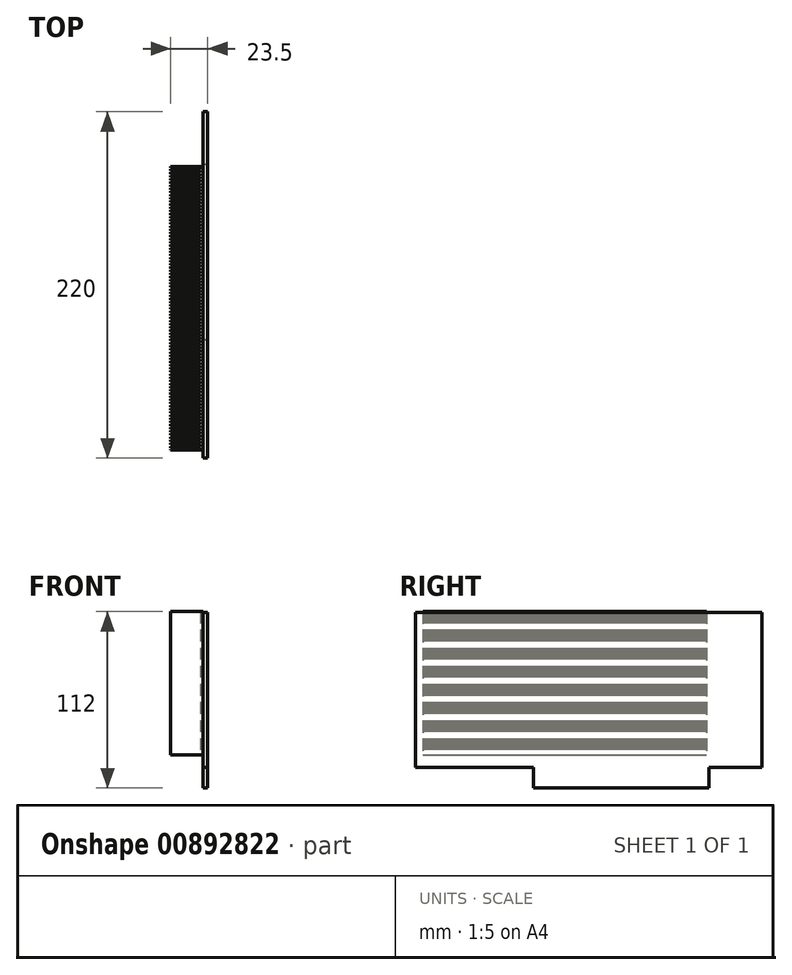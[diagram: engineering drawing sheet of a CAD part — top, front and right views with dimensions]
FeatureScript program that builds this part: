
annotation { "Feature Type Name" : "Feature", "Feature Type Description" : "" }
export const myFeature = defineFeature(function(context is Context, id is Id, definition is map)
    precondition{}
    {
        {
            var Q0;
            Q0=qCreatedBy(makeId("Right.planeOp"),FACE);
            var sketch = newSketch(context, id + "F0", { "sketchPlane" : qUnion([Q0])});
            skLineSegment(sketch, "E0.bottom", {"start": v(-110, 55.75) * mm, "end": v(110, 55.75) * mm});
            skLineSegment(sketch, "E0.top", {"start": v(-35, -55.75) * mm, "end": v(76.5, -55.75) * mm});
            skLineSegment(sketch, "E0.left", {"start": v(-110, 55.75) * mm, "end": v(-110, -42.75) * mm});
            skLineSegment(sketch, "E0.right", {"start": v(110, 55.75) * mm, "end": v(110, -42.75) * mm});
            skPoint(sketch, "E0.middle", {"position": v(0, 0) * mm});
            skLineSegment(sketch, "E1", {"start": v(-110, -42.75) * mm, "end": v(-35, -42.75) * mm});
            skLineSegment(sketch, "E2", {"start": v(-35, -42.75) * mm, "end": v(-35, -55.75) * mm});
            skLineSegment(sketch, "E3", {"start": v(76.5, -55.75) * mm, "end": v(76.5, -42.75) * mm});
            skLineSegment(sketch, "E4", {"start": v(76.5, -42.75) * mm, "end": v(110, -42.75) * mm});
            skLineSegment(sketch, "E5.bottom", {"start": v(-105, 56.25) * mm, "end": v(75, 56.25) * mm});
            skLineSegment(sketch, "E5.top", {"start": v(-105, -34.75) * mm, "end": v(75, -34.75) * mm});
            skLineSegment(sketch, "E5.left", {"start": v(-105, 56.25) * mm, "end": v(-105, -34.75) * mm});
            skLineSegment(sketch, "E5.right", {"start": v(75, 56.25) * mm, "end": v(75, -34.75) * mm});
            skSolve(sketch);
        }
        {
            var Q0;
            Q0=makeQuery(id+"F0.imprint","IMPRINT",FACE,{"disambiguationData":[TD([[makeQuery(id+"F0.imprint","IMPRINT",EDGE,{"derivedFrom":sQuery(id+"F0.wireOp",EDGE,"E0.top")}),1.0]])]});
            extrude(context, id + "F1", {"entities" : qUnion([Q0]), "depth" : 3 * mm, "offsetDistance" : 25 * mm});
        }
        {
            var Q0;
            {var subQ5=sQuery(id+"F0.wireOp",EDGE,"E5.top");Q0=makeQuery(id+"F0.imprint","IMPRINT",FACE,{"disambiguationData":[TD([[makeQuery(id+"F0.imprint","IMPRINT",EDGE,{"derivedFrom":subQ5}),1.0]])]});}
            extrude(context, id + "F2", {"entities" : qUnion([Q0]), "operationType" : NewBodyOperationType.ADD, "depth" : 3 * mm, "offsetDistance" : 25 * mm});
        }
        {
            var Q0;
            {var subQ5=sQuery(id+"F0.wireOp",EDGE,"E5.bottom");Q0=makeQuery(id+"F0.imprint","IMPRINT",FACE,{"disambiguationData":[TD([[makeQuery(id+"F0.imprint","IMPRINT",EDGE,{"derivedFrom":subQ5}),-1.0]])]});}
            var Q1;
            {var subQ5=sQuery(id+"F0.wireOp",EDGE,"E5.top");Q1=makeQuery(id+"F0.imprint","IMPRINT",FACE,{"disambiguationData":[TD([[makeQuery(id+"F0.imprint","IMPRINT",EDGE,{"derivedFrom":subQ5}),1.0]])]});}
            extrude(context, id + "F3", {"entities" : qUnion([Q0, Q1]), "operationType" : NewBodyOperationType.ADD, "depth" : -20.5 * mm, "offsetDistance" : 25 * mm});
        }
        {
            var Q0;
            Q0=makeQuery(id+"F3.opExtrude","CAP_FACE",FACE,{"disambiguationData":[OSD([sQuery(id+"F0.wireOp",EDGE,"E5.bottom"),sQuery(id+"F0.wireOp",EDGE,"E5.top"),sQuery(id+"F0.wireOp",EDGE,"E5.left"),sQuery(id+"F0.wireOp",EDGE,"E5.right")])],"isStart":false});
            var sketch = newSketch(context, id + "F4", { "sketchPlane" : qUnion([Q0])});
            skLineSegment(sketch, "E6.bottom", {"start": v(-74.5, 56.25) * mm, "end": v(-73.5, 56.25) * mm});
            skLineSegment(sketch, "E6.top", {"start": v(-74.5, -34.75) * mm, "end": v(-73.5, -34.75) * mm});
            skLineSegment(sketch, "E6.left", {"start": v(-74.5, 56.25) * mm, "end": v(-74.5, -34.75) * mm});
            skLineSegment(sketch, "E6.right", {"start": v(-73.5, 56.25) * mm, "end": v(-73.5, -34.75) * mm});
            skLineSegment(sketch, "E7.1.0.0", {"start": v(-72.5, 56.25) * mm, "end": v(-71.5, 56.25) * mm});
            skLineSegment(sketch, "E7.1.0.1", {"start": v(-72.5, -34.75) * mm, "end": v(-71.5, -34.75) * mm});
            skLineSegment(sketch, "E7.1.0.2", {"start": v(-72.5, 56.25) * mm, "end": v(-72.5, -34.75) * mm});
            skLineSegment(sketch, "E7.1.0.3", {"start": v(-71.5, 56.25) * mm, "end": v(-71.5, -34.75) * mm});
            skLineSegment(sketch, "E7.2.0.0", {"start": v(-70.5, 56.25) * mm, "end": v(-69.5, 56.25) * mm});
            skLineSegment(sketch, "E7.2.0.1", {"start": v(-70.5, -34.75) * mm, "end": v(-69.5, -34.75) * mm});
            skLineSegment(sketch, "E7.2.0.2", {"start": v(-70.5, 56.25) * mm, "end": v(-70.5, -34.75) * mm});
            skLineSegment(sketch, "E7.2.0.3", {"start": v(-69.5, 56.25) * mm, "end": v(-69.5, -34.75) * mm});
            skLineSegment(sketch, "E7.3.0.0", {"start": v(-68.5, 56.25) * mm, "end": v(-67.5, 56.25) * mm});
            skLineSegment(sketch, "E7.3.0.1", {"start": v(-68.5, -34.75) * mm, "end": v(-67.5, -34.75) * mm});
            skLineSegment(sketch, "E7.3.0.2", {"start": v(-68.5, 56.25) * mm, "end": v(-68.5, -34.75) * mm});
            skLineSegment(sketch, "E7.3.0.3", {"start": v(-67.5, 56.25) * mm, "end": v(-67.5, -34.75) * mm});
            skLineSegment(sketch, "E7.4.0.0", {"start": v(-66.5, 56.25) * mm, "end": v(-65.5, 56.25) * mm});
            skLineSegment(sketch, "E7.4.0.1", {"start": v(-66.5, -34.75) * mm, "end": v(-65.5, -34.75) * mm});
            skLineSegment(sketch, "E7.4.0.2", {"start": v(-66.5, 56.25) * mm, "end": v(-66.5, -34.75) * mm});
            skLineSegment(sketch, "E7.4.0.3", {"start": v(-65.5, 56.25) * mm, "end": v(-65.5, -34.75) * mm});
            skLineSegment(sketch, "E7.5.0.0", {"start": v(-64.5, 56.25) * mm, "end": v(-63.5, 56.25) * mm});
            skLineSegment(sketch, "E7.5.0.1", {"start": v(-64.5, -34.75) * mm, "end": v(-63.5, -34.75) * mm});
            skLineSegment(sketch, "E7.5.0.2", {"start": v(-64.5, 56.25) * mm, "end": v(-64.5, -34.75) * mm});
            skLineSegment(sketch, "E7.5.0.3", {"start": v(-63.5, 56.25) * mm, "end": v(-63.5, -34.75) * mm});
            skLineSegment(sketch, "E7.6.0.0", {"start": v(-62.5, 56.25) * mm, "end": v(-61.5, 56.25) * mm});
            skLineSegment(sketch, "E7.6.0.1", {"start": v(-62.5, -34.75) * mm, "end": v(-61.5, -34.75) * mm});
            skLineSegment(sketch, "E7.6.0.2", {"start": v(-62.5, 56.25) * mm, "end": v(-62.5, -34.75) * mm});
            skLineSegment(sketch, "E7.6.0.3", {"start": v(-61.5, 56.25) * mm, "end": v(-61.5, -34.75) * mm});
            skLineSegment(sketch, "E7.7.0.0", {"start": v(-60.5, 56.25) * mm, "end": v(-59.5, 56.25) * mm});
            skLineSegment(sketch, "E7.7.0.1", {"start": v(-60.5, -34.75) * mm, "end": v(-59.5, -34.75) * mm});
            skLineSegment(sketch, "E7.7.0.2", {"start": v(-60.5, 56.25) * mm, "end": v(-60.5, -34.75) * mm});
            skLineSegment(sketch, "E7.7.0.3", {"start": v(-59.5, 56.25) * mm, "end": v(-59.5, -34.75) * mm});
            skLineSegment(sketch, "E7.8.0.0", {"start": v(-58.5, 56.25) * mm, "end": v(-57.5, 56.25) * mm});
            skLineSegment(sketch, "E7.8.0.1", {"start": v(-58.5, -34.75) * mm, "end": v(-57.5, -34.75) * mm});
            skLineSegment(sketch, "E7.8.0.2", {"start": v(-58.5, 56.25) * mm, "end": v(-58.5, -34.75) * mm});
            skLineSegment(sketch, "E7.8.0.3", {"start": v(-57.5, 56.25) * mm, "end": v(-57.5, -34.75) * mm});
            skLineSegment(sketch, "E7.9.0.0", {"start": v(-56.5, 56.25) * mm, "end": v(-55.5, 56.25) * mm});
            skLineSegment(sketch, "E7.9.0.1", {"start": v(-56.5, -34.75) * mm, "end": v(-55.5, -34.75) * mm});
            skLineSegment(sketch, "E7.9.0.2", {"start": v(-56.5, 56.25) * mm, "end": v(-56.5, -34.75) * mm});
            skLineSegment(sketch, "E7.9.0.3", {"start": v(-55.5, 56.25) * mm, "end": v(-55.5, -34.75) * mm});
            skLineSegment(sketch, "E7.10.0.0", {"start": v(-54.5, 56.25) * mm, "end": v(-53.5, 56.25) * mm});
            skLineSegment(sketch, "E7.10.0.1", {"start": v(-54.5, -34.75) * mm, "end": v(-53.5, -34.75) * mm});
            skLineSegment(sketch, "E7.10.0.2", {"start": v(-54.5, 56.25) * mm, "end": v(-54.5, -34.75) * mm});
            skLineSegment(sketch, "E7.10.0.3", {"start": v(-53.5, 56.25) * mm, "end": v(-53.5, -34.75) * mm});
            skLineSegment(sketch, "E7.11.0.0", {"start": v(-52.5, 56.25) * mm, "end": v(-51.5, 56.25) * mm});
            skLineSegment(sketch, "E7.11.0.1", {"start": v(-52.5, -34.75) * mm, "end": v(-51.5, -34.75) * mm});
            skLineSegment(sketch, "E7.11.0.2", {"start": v(-52.5, 56.25) * mm, "end": v(-52.5, -34.75) * mm});
            skLineSegment(sketch, "E7.11.0.3", {"start": v(-51.5, 56.25) * mm, "end": v(-51.5, -34.75) * mm});
            skLineSegment(sketch, "E7.12.0.0", {"start": v(-50.5, 56.25) * mm, "end": v(-49.5, 56.25) * mm});
            skLineSegment(sketch, "E7.12.0.1", {"start": v(-50.5, -34.75) * mm, "end": v(-49.5, -34.75) * mm});
            skLineSegment(sketch, "E7.12.0.2", {"start": v(-50.5, 56.25) * mm, "end": v(-50.5, -34.75) * mm});
            skLineSegment(sketch, "E7.12.0.3", {"start": v(-49.5, 56.25) * mm, "end": v(-49.5, -34.75) * mm});
            skLineSegment(sketch, "E7.13.0.0", {"start": v(-48.5, 56.25) * mm, "end": v(-47.5, 56.25) * mm});
            skLineSegment(sketch, "E7.13.0.1", {"start": v(-48.5, -34.75) * mm, "end": v(-47.5, -34.75) * mm});
            skLineSegment(sketch, "E7.13.0.2", {"start": v(-48.5, 56.25) * mm, "end": v(-48.5, -34.75) * mm});
            skLineSegment(sketch, "E7.13.0.3", {"start": v(-47.5, 56.25) * mm, "end": v(-47.5, -34.75) * mm});
            skLineSegment(sketch, "E7.14.0.0", {"start": v(-46.5, 56.25) * mm, "end": v(-45.5, 56.25) * mm});
            skLineSegment(sketch, "E7.14.0.1", {"start": v(-46.5, -34.75) * mm, "end": v(-45.5, -34.75) * mm});
            skLineSegment(sketch, "E7.14.0.2", {"start": v(-46.5, 56.25) * mm, "end": v(-46.5, -34.75) * mm});
            skLineSegment(sketch, "E7.14.0.3", {"start": v(-45.5, 56.25) * mm, "end": v(-45.5, -34.75) * mm});
            skLineSegment(sketch, "E7.15.0.0", {"start": v(-44.5, 56.25) * mm, "end": v(-43.5, 56.25) * mm});
            skLineSegment(sketch, "E7.15.0.1", {"start": v(-44.5, -34.75) * mm, "end": v(-43.5, -34.75) * mm});
            skLineSegment(sketch, "E7.15.0.2", {"start": v(-44.5, 56.25) * mm, "end": v(-44.5, -34.75) * mm});
            skLineSegment(sketch, "E7.15.0.3", {"start": v(-43.5, 56.25) * mm, "end": v(-43.5, -34.75) * mm});
            skLineSegment(sketch, "E7.16.0.0", {"start": v(-42.5, 56.25) * mm, "end": v(-41.5, 56.25) * mm});
            skLineSegment(sketch, "E7.16.0.1", {"start": v(-42.5, -34.75) * mm, "end": v(-41.5, -34.75) * mm});
            skLineSegment(sketch, "E7.16.0.2", {"start": v(-42.5, 56.25) * mm, "end": v(-42.5, -34.75) * mm});
            skLineSegment(sketch, "E7.16.0.3", {"start": v(-41.5, 56.25) * mm, "end": v(-41.5, -34.75) * mm});
            skLineSegment(sketch, "E7.17.0.0", {"start": v(-40.5, 56.25) * mm, "end": v(-39.5, 56.25) * mm});
            skLineSegment(sketch, "E7.17.0.1", {"start": v(-40.5, -34.75) * mm, "end": v(-39.5, -34.75) * mm});
            skLineSegment(sketch, "E7.17.0.2", {"start": v(-40.5, 56.25) * mm, "end": v(-40.5, -34.75) * mm});
            skLineSegment(sketch, "E7.17.0.3", {"start": v(-39.5, 56.25) * mm, "end": v(-39.5, -34.75) * mm});
            skLineSegment(sketch, "E7.18.0.0", {"start": v(-38.5, 56.25) * mm, "end": v(-37.5, 56.25) * mm});
            skLineSegment(sketch, "E7.18.0.1", {"start": v(-38.5, -34.75) * mm, "end": v(-37.5, -34.75) * mm});
            skLineSegment(sketch, "E7.18.0.2", {"start": v(-38.5, 56.25) * mm, "end": v(-38.5, -34.75) * mm});
            skLineSegment(sketch, "E7.18.0.3", {"start": v(-37.5, 56.25) * mm, "end": v(-37.5, -34.75) * mm});
            skLineSegment(sketch, "E7.19.0.0", {"start": v(-36.5, 56.25) * mm, "end": v(-35.5, 56.25) * mm});
            skLineSegment(sketch, "E7.19.0.1", {"start": v(-36.5, -34.75) * mm, "end": v(-35.5, -34.75) * mm});
            skLineSegment(sketch, "E7.19.0.2", {"start": v(-36.5, 56.25) * mm, "end": v(-36.5, -34.75) * mm});
            skLineSegment(sketch, "E7.19.0.3", {"start": v(-35.5, 56.25) * mm, "end": v(-35.5, -34.75) * mm});
            skLineSegment(sketch, "E7.20.0.0", {"start": v(-34.5, 56.25) * mm, "end": v(-33.5, 56.25) * mm});
            skLineSegment(sketch, "E7.20.0.1", {"start": v(-34.5, -34.75) * mm, "end": v(-33.5, -34.75) * mm});
            skLineSegment(sketch, "E7.20.0.2", {"start": v(-34.5, 56.25) * mm, "end": v(-34.5, -34.75) * mm});
            skLineSegment(sketch, "E7.20.0.3", {"start": v(-33.5, 56.25) * mm, "end": v(-33.5, -34.75) * mm});
            skLineSegment(sketch, "E7.21.0.0", {"start": v(-32.5, 56.25) * mm, "end": v(-31.5, 56.25) * mm});
            skLineSegment(sketch, "E7.21.0.1", {"start": v(-32.5, -34.75) * mm, "end": v(-31.5, -34.75) * mm});
            skLineSegment(sketch, "E7.21.0.2", {"start": v(-32.5, 56.25) * mm, "end": v(-32.5, -34.75) * mm});
            skLineSegment(sketch, "E7.21.0.3", {"start": v(-31.5, 56.25) * mm, "end": v(-31.5, -34.75) * mm});
            skLineSegment(sketch, "E7.22.0.0", {"start": v(-30.5, 56.25) * mm, "end": v(-29.5, 56.25) * mm});
            skLineSegment(sketch, "E7.22.0.1", {"start": v(-30.5, -34.75) * mm, "end": v(-29.5, -34.75) * mm});
            skLineSegment(sketch, "E7.22.0.2", {"start": v(-30.5, 56.25) * mm, "end": v(-30.5, -34.75) * mm});
            skLineSegment(sketch, "E7.22.0.3", {"start": v(-29.5, 56.25) * mm, "end": v(-29.5, -34.75) * mm});
            skLineSegment(sketch, "E7.23.0.0", {"start": v(-28.5, 56.25) * mm, "end": v(-27.5, 56.25) * mm});
            skLineSegment(sketch, "E7.23.0.1", {"start": v(-28.5, -34.75) * mm, "end": v(-27.5, -34.75) * mm});
            skLineSegment(sketch, "E7.23.0.2", {"start": v(-28.5, 56.25) * mm, "end": v(-28.5, -34.75) * mm});
            skLineSegment(sketch, "E7.23.0.3", {"start": v(-27.5, 56.25) * mm, "end": v(-27.5, -34.75) * mm});
            skLineSegment(sketch, "E7.24.0.0", {"start": v(-26.5, 56.25) * mm, "end": v(-25.5, 56.25) * mm});
            skLineSegment(sketch, "E7.24.0.1", {"start": v(-26.5, -34.75) * mm, "end": v(-25.5, -34.75) * mm});
            skLineSegment(sketch, "E7.24.0.2", {"start": v(-26.5, 56.25) * mm, "end": v(-26.5, -34.75) * mm});
            skLineSegment(sketch, "E7.24.0.3", {"start": v(-25.5, 56.25) * mm, "end": v(-25.5, -34.75) * mm});
            skLineSegment(sketch, "E7.25.0.0", {"start": v(-24.5, 56.25) * mm, "end": v(-23.5, 56.25) * mm});
            skLineSegment(sketch, "E7.25.0.1", {"start": v(-24.5, -34.75) * mm, "end": v(-23.5, -34.75) * mm});
            skLineSegment(sketch, "E7.25.0.2", {"start": v(-24.5, 56.25) * mm, "end": v(-24.5, -34.75) * mm});
            skLineSegment(sketch, "E7.25.0.3", {"start": v(-23.5, 56.25) * mm, "end": v(-23.5, -34.75) * mm});
            skLineSegment(sketch, "E7.26.0.0", {"start": v(-22.5, 56.25) * mm, "end": v(-21.5, 56.25) * mm});
            skLineSegment(sketch, "E7.26.0.1", {"start": v(-22.5, -34.75) * mm, "end": v(-21.5, -34.75) * mm});
            skLineSegment(sketch, "E7.26.0.2", {"start": v(-22.5, 56.25) * mm, "end": v(-22.5, -34.75) * mm});
            skLineSegment(sketch, "E7.26.0.3", {"start": v(-21.5, 56.25) * mm, "end": v(-21.5, -34.75) * mm});
            skLineSegment(sketch, "E7.27.0.0", {"start": v(-20.5, 56.25) * mm, "end": v(-19.5, 56.25) * mm});
            skLineSegment(sketch, "E7.27.0.1", {"start": v(-20.5, -34.75) * mm, "end": v(-19.5, -34.75) * mm});
            skLineSegment(sketch, "E7.27.0.2", {"start": v(-20.5, 56.25) * mm, "end": v(-20.5, -34.75) * mm});
            skLineSegment(sketch, "E7.27.0.3", {"start": v(-19.5, 56.25) * mm, "end": v(-19.5, -34.75) * mm});
            skLineSegment(sketch, "E7.28.0.0", {"start": v(-18.5, 56.25) * mm, "end": v(-17.5, 56.25) * mm});
            skLineSegment(sketch, "E7.28.0.1", {"start": v(-18.5, -34.75) * mm, "end": v(-17.5, -34.75) * mm});
            skLineSegment(sketch, "E7.28.0.2", {"start": v(-18.5, 56.25) * mm, "end": v(-18.5, -34.75) * mm});
            skLineSegment(sketch, "E7.28.0.3", {"start": v(-17.5, 56.25) * mm, "end": v(-17.5, -34.75) * mm});
            skLineSegment(sketch, "E7.29.0.0", {"start": v(-16.5, 56.25) * mm, "end": v(-15.5, 56.25) * mm});
            skLineSegment(sketch, "E7.29.0.1", {"start": v(-16.5, -34.75) * mm, "end": v(-15.5, -34.75) * mm});
            skLineSegment(sketch, "E7.29.0.2", {"start": v(-16.5, 56.25) * mm, "end": v(-16.5, -34.75) * mm});
            skLineSegment(sketch, "E7.29.0.3", {"start": v(-15.5, 56.25) * mm, "end": v(-15.5, -34.75) * mm});
            skLineSegment(sketch, "E7.30.0.0", {"start": v(-14.5, 56.25) * mm, "end": v(-13.5, 56.25) * mm});
            skLineSegment(sketch, "E7.30.0.1", {"start": v(-14.5, -34.75) * mm, "end": v(-13.5, -34.75) * mm});
            skLineSegment(sketch, "E7.30.0.2", {"start": v(-14.5, 56.25) * mm, "end": v(-14.5, -34.75) * mm});
            skLineSegment(sketch, "E7.30.0.3", {"start": v(-13.5, 56.25) * mm, "end": v(-13.5, -34.75) * mm});
            skLineSegment(sketch, "E7.31.0.0", {"start": v(-12.5, 56.25) * mm, "end": v(-11.5, 56.25) * mm});
            skLineSegment(sketch, "E7.31.0.1", {"start": v(-12.5, -34.75) * mm, "end": v(-11.5, -34.75) * mm});
            skLineSegment(sketch, "E7.31.0.2", {"start": v(-12.5, 56.25) * mm, "end": v(-12.5, -34.75) * mm});
            skLineSegment(sketch, "E7.31.0.3", {"start": v(-11.5, 56.25) * mm, "end": v(-11.5, -34.75) * mm});
            skLineSegment(sketch, "E7.32.0.0", {"start": v(-10.5, 56.25) * mm, "end": v(-9.5, 56.25) * mm});
            skLineSegment(sketch, "E7.32.0.1", {"start": v(-10.5, -34.75) * mm, "end": v(-9.5, -34.75) * mm});
            skLineSegment(sketch, "E7.32.0.2", {"start": v(-10.5, 56.25) * mm, "end": v(-10.5, -34.75) * mm});
            skLineSegment(sketch, "E7.32.0.3", {"start": v(-9.5, 56.25) * mm, "end": v(-9.5, -34.75) * mm});
            skLineSegment(sketch, "E7.33.0.0", {"start": v(-8.5, 56.25) * mm, "end": v(-7.5, 56.25) * mm});
            skLineSegment(sketch, "E7.33.0.1", {"start": v(-8.5, -34.75) * mm, "end": v(-7.5, -34.75) * mm});
            skLineSegment(sketch, "E7.33.0.2", {"start": v(-8.5, 56.25) * mm, "end": v(-8.5, -34.75) * mm});
            skLineSegment(sketch, "E7.33.0.3", {"start": v(-7.5, 56.25) * mm, "end": v(-7.5, -34.75) * mm});
            skLineSegment(sketch, "E7.34.0.0", {"start": v(-6.5, 56.25) * mm, "end": v(-5.5, 56.25) * mm});
            skLineSegment(sketch, "E7.34.0.1", {"start": v(-6.5, -34.75) * mm, "end": v(-5.5, -34.75) * mm});
            skLineSegment(sketch, "E7.34.0.2", {"start": v(-6.5, 56.25) * mm, "end": v(-6.5, -34.75) * mm});
            skLineSegment(sketch, "E7.34.0.3", {"start": v(-5.5, 56.25) * mm, "end": v(-5.5, -34.75) * mm});
            skLineSegment(sketch, "E7.35.0.0", {"start": v(-4.5, 56.25) * mm, "end": v(-3.5, 56.25) * mm});
            skLineSegment(sketch, "E7.35.0.1", {"start": v(-4.5, -34.75) * mm, "end": v(-3.5, -34.75) * mm});
            skLineSegment(sketch, "E7.35.0.2", {"start": v(-4.5, 56.25) * mm, "end": v(-4.5, -34.75) * mm});
            skLineSegment(sketch, "E7.35.0.3", {"start": v(-3.5, 56.25) * mm, "end": v(-3.5, -34.75) * mm});
            skLineSegment(sketch, "E7.36.0.0", {"start": v(-2.5, 56.25) * mm, "end": v(-1.5, 56.25) * mm});
            skLineSegment(sketch, "E7.36.0.1", {"start": v(-2.5, -34.75) * mm, "end": v(-1.5, -34.75) * mm});
            skLineSegment(sketch, "E7.36.0.2", {"start": v(-2.5, 56.25) * mm, "end": v(-2.5, -34.75) * mm});
            skLineSegment(sketch, "E7.36.0.3", {"start": v(-1.5, 56.25) * mm, "end": v(-1.5, -34.75) * mm});
            skLineSegment(sketch, "E7.37.0.0", {"start": v(-0.5, 56.25) * mm, "end": v(0.5, 56.25) * mm});
            skLineSegment(sketch, "E7.37.0.1", {"start": v(-0.5, -34.75) * mm, "end": v(0.5, -34.75) * mm});
            skLineSegment(sketch, "E7.37.0.2", {"start": v(-0.5, 56.25) * mm, "end": v(-0.5, -34.75) * mm});
            skLineSegment(sketch, "E7.37.0.3", {"start": v(0.5, 56.25) * mm, "end": v(0.5, -34.75) * mm});
            skLineSegment(sketch, "E7.38.0.0", {"start": v(1.5, 56.25) * mm, "end": v(2.5, 56.25) * mm});
            skLineSegment(sketch, "E7.38.0.1", {"start": v(1.5, -34.75) * mm, "end": v(2.5, -34.75) * mm});
            skLineSegment(sketch, "E7.38.0.2", {"start": v(1.5, 56.25) * mm, "end": v(1.5, -34.75) * mm});
            skLineSegment(sketch, "E7.38.0.3", {"start": v(2.5, 56.25) * mm, "end": v(2.5, -34.75) * mm});
            skLineSegment(sketch, "E7.39.0.0", {"start": v(3.5, 56.25) * mm, "end": v(4.5, 56.25) * mm});
            skLineSegment(sketch, "E7.39.0.1", {"start": v(3.5, -34.75) * mm, "end": v(4.5, -34.75) * mm});
            skLineSegment(sketch, "E7.39.0.2", {"start": v(3.5, 56.25) * mm, "end": v(3.5, -34.75) * mm});
            skLineSegment(sketch, "E7.39.0.3", {"start": v(4.5, 56.25) * mm, "end": v(4.5, -34.75) * mm});
            skLineSegment(sketch, "E7.40.0.0", {"start": v(5.5, 56.25) * mm, "end": v(6.5, 56.25) * mm});
            skLineSegment(sketch, "E7.40.0.1", {"start": v(5.5, -34.75) * mm, "end": v(6.5, -34.75) * mm});
            skLineSegment(sketch, "E7.40.0.2", {"start": v(5.5, 56.25) * mm, "end": v(5.5, -34.75) * mm});
            skLineSegment(sketch, "E7.40.0.3", {"start": v(6.5, 56.25) * mm, "end": v(6.5, -34.75) * mm});
            skLineSegment(sketch, "E7.41.0.0", {"start": v(7.5, 56.25) * mm, "end": v(8.5, 56.25) * mm});
            skLineSegment(sketch, "E7.41.0.1", {"start": v(7.5, -34.75) * mm, "end": v(8.5, -34.75) * mm});
            skLineSegment(sketch, "E7.41.0.2", {"start": v(7.5, 56.25) * mm, "end": v(7.5, -34.75) * mm});
            skLineSegment(sketch, "E7.41.0.3", {"start": v(8.5, 56.25) * mm, "end": v(8.5, -34.75) * mm});
            skLineSegment(sketch, "E7.42.0.0", {"start": v(9.5, 56.25) * mm, "end": v(10.5, 56.25) * mm});
            skLineSegment(sketch, "E7.42.0.1", {"start": v(9.5, -34.75) * mm, "end": v(10.5, -34.75) * mm});
            skLineSegment(sketch, "E7.42.0.2", {"start": v(9.5, 56.25) * mm, "end": v(9.5, -34.75) * mm});
            skLineSegment(sketch, "E7.42.0.3", {"start": v(10.5, 56.25) * mm, "end": v(10.5, -34.75) * mm});
            skLineSegment(sketch, "E7.43.0.0", {"start": v(11.5, 56.25) * mm, "end": v(12.5, 56.25) * mm});
            skLineSegment(sketch, "E7.43.0.1", {"start": v(11.5, -34.75) * mm, "end": v(12.5, -34.75) * mm});
            skLineSegment(sketch, "E7.43.0.2", {"start": v(11.5, 56.25) * mm, "end": v(11.5, -34.75) * mm});
            skLineSegment(sketch, "E7.43.0.3", {"start": v(12.5, 56.25) * mm, "end": v(12.5, -34.75) * mm});
            skLineSegment(sketch, "E7.44.0.0", {"start": v(13.5, 56.25) * mm, "end": v(14.5, 56.25) * mm});
            skLineSegment(sketch, "E7.44.0.1", {"start": v(13.5, -34.75) * mm, "end": v(14.5, -34.75) * mm});
            skLineSegment(sketch, "E7.44.0.2", {"start": v(13.5, 56.25) * mm, "end": v(13.5, -34.75) * mm});
            skLineSegment(sketch, "E7.44.0.3", {"start": v(14.5, 56.25) * mm, "end": v(14.5, -34.75) * mm});
            skLineSegment(sketch, "E7.45.0.0", {"start": v(15.5, 56.25) * mm, "end": v(16.5, 56.25) * mm});
            skLineSegment(sketch, "E7.45.0.1", {"start": v(15.5, -34.75) * mm, "end": v(16.5, -34.75) * mm});
            skLineSegment(sketch, "E7.45.0.2", {"start": v(15.5, 56.25) * mm, "end": v(15.5, -34.75) * mm});
            skLineSegment(sketch, "E7.45.0.3", {"start": v(16.5, 56.25) * mm, "end": v(16.5, -34.75) * mm});
            skLineSegment(sketch, "E7.46.0.0", {"start": v(17.5, 56.25) * mm, "end": v(18.5, 56.25) * mm});
            skLineSegment(sketch, "E7.46.0.1", {"start": v(17.5, -34.75) * mm, "end": v(18.5, -34.75) * mm});
            skLineSegment(sketch, "E7.46.0.2", {"start": v(17.5, 56.25) * mm, "end": v(17.5, -34.75) * mm});
            skLineSegment(sketch, "E7.46.0.3", {"start": v(18.5, 56.25) * mm, "end": v(18.5, -34.75) * mm});
            skLineSegment(sketch, "E7.47.0.0", {"start": v(19.5, 56.25) * mm, "end": v(20.5, 56.25) * mm});
            skLineSegment(sketch, "E7.47.0.1", {"start": v(19.5, -34.75) * mm, "end": v(20.5, -34.75) * mm});
            skLineSegment(sketch, "E7.47.0.2", {"start": v(19.5, 56.25) * mm, "end": v(19.5, -34.75) * mm});
            skLineSegment(sketch, "E7.47.0.3", {"start": v(20.5, 56.25) * mm, "end": v(20.5, -34.75) * mm});
            skLineSegment(sketch, "E7.48.0.0", {"start": v(21.5, 56.25) * mm, "end": v(22.5, 56.25) * mm});
            skLineSegment(sketch, "E7.48.0.1", {"start": v(21.5, -34.75) * mm, "end": v(22.5, -34.75) * mm});
            skLineSegment(sketch, "E7.48.0.2", {"start": v(21.5, 56.25) * mm, "end": v(21.5, -34.75) * mm});
            skLineSegment(sketch, "E7.48.0.3", {"start": v(22.5, 56.25) * mm, "end": v(22.5, -34.75) * mm});
            skLineSegment(sketch, "E7.49.0.0", {"start": v(23.5, 56.25) * mm, "end": v(24.5, 56.25) * mm});
            skLineSegment(sketch, "E7.49.0.1", {"start": v(23.5, -34.75) * mm, "end": v(24.5, -34.75) * mm});
            skLineSegment(sketch, "E7.49.0.2", {"start": v(23.5, 56.25) * mm, "end": v(23.5, -34.75) * mm});
            skLineSegment(sketch, "E7.49.0.3", {"start": v(24.5, 56.25) * mm, "end": v(24.5, -34.75) * mm});
            skLineSegment(sketch, "E7.50.0.0", {"start": v(25.5, 56.25) * mm, "end": v(26.5, 56.25) * mm});
            skLineSegment(sketch, "E7.50.0.1", {"start": v(25.5, -34.75) * mm, "end": v(26.5, -34.75) * mm});
            skLineSegment(sketch, "E7.50.0.2", {"start": v(25.5, 56.25) * mm, "end": v(25.5, -34.75) * mm});
            skLineSegment(sketch, "E7.50.0.3", {"start": v(26.5, 56.25) * mm, "end": v(26.5, -34.75) * mm});
            skLineSegment(sketch, "E7.51.0.0", {"start": v(27.5, 56.25) * mm, "end": v(28.5, 56.25) * mm});
            skLineSegment(sketch, "E7.51.0.1", {"start": v(27.5, -34.75) * mm, "end": v(28.5, -34.75) * mm});
            skLineSegment(sketch, "E7.51.0.2", {"start": v(27.5, 56.25) * mm, "end": v(27.5, -34.75) * mm});
            skLineSegment(sketch, "E7.51.0.3", {"start": v(28.5, 56.25) * mm, "end": v(28.5, -34.75) * mm});
            skLineSegment(sketch, "E7.52.0.0", {"start": v(29.5, 56.25) * mm, "end": v(30.5, 56.25) * mm});
            skLineSegment(sketch, "E7.52.0.1", {"start": v(29.5, -34.75) * mm, "end": v(30.5, -34.75) * mm});
            skLineSegment(sketch, "E7.52.0.2", {"start": v(29.5, 56.25) * mm, "end": v(29.5, -34.75) * mm});
            skLineSegment(sketch, "E7.52.0.3", {"start": v(30.5, 56.25) * mm, "end": v(30.5, -34.75) * mm});
            skLineSegment(sketch, "E7.53.0.0", {"start": v(31.5, 56.25) * mm, "end": v(32.5, 56.25) * mm});
            skLineSegment(sketch, "E7.53.0.1", {"start": v(31.5, -34.75) * mm, "end": v(32.5, -34.75) * mm});
            skLineSegment(sketch, "E7.53.0.2", {"start": v(31.5, 56.25) * mm, "end": v(31.5, -34.75) * mm});
            skLineSegment(sketch, "E7.53.0.3", {"start": v(32.5, 56.25) * mm, "end": v(32.5, -34.75) * mm});
            skLineSegment(sketch, "E7.54.0.0", {"start": v(33.5, 56.25) * mm, "end": v(34.5, 56.25) * mm});
            skLineSegment(sketch, "E7.54.0.1", {"start": v(33.5, -34.75) * mm, "end": v(34.5, -34.75) * mm});
            skLineSegment(sketch, "E7.54.0.2", {"start": v(33.5, 56.25) * mm, "end": v(33.5, -34.75) * mm});
            skLineSegment(sketch, "E7.54.0.3", {"start": v(34.5, 56.25) * mm, "end": v(34.5, -34.75) * mm});
            skLineSegment(sketch, "E7.55.0.0", {"start": v(35.5, 56.25) * mm, "end": v(36.5, 56.25) * mm});
            skLineSegment(sketch, "E7.55.0.1", {"start": v(35.5, -34.75) * mm, "end": v(36.5, -34.75) * mm});
            skLineSegment(sketch, "E7.55.0.2", {"start": v(35.5, 56.25) * mm, "end": v(35.5, -34.75) * mm});
            skLineSegment(sketch, "E7.55.0.3", {"start": v(36.5, 56.25) * mm, "end": v(36.5, -34.75) * mm});
            skLineSegment(sketch, "E7.56.0.0", {"start": v(37.5, 56.25) * mm, "end": v(38.5, 56.25) * mm});
            skLineSegment(sketch, "E7.56.0.1", {"start": v(37.5, -34.75) * mm, "end": v(38.5, -34.75) * mm});
            skLineSegment(sketch, "E7.56.0.2", {"start": v(37.5, 56.25) * mm, "end": v(37.5, -34.75) * mm});
            skLineSegment(sketch, "E7.56.0.3", {"start": v(38.5, 56.25) * mm, "end": v(38.5, -34.75) * mm});
            skLineSegment(sketch, "E7.57.0.0", {"start": v(39.5, 56.25) * mm, "end": v(40.5, 56.25) * mm});
            skLineSegment(sketch, "E7.57.0.1", {"start": v(39.5, -34.75) * mm, "end": v(40.5, -34.75) * mm});
            skLineSegment(sketch, "E7.57.0.2", {"start": v(39.5, 56.25) * mm, "end": v(39.5, -34.75) * mm});
            skLineSegment(sketch, "E7.57.0.3", {"start": v(40.5, 56.25) * mm, "end": v(40.5, -34.75) * mm});
            skLineSegment(sketch, "E7.58.0.0", {"start": v(41.5, 56.25) * mm, "end": v(42.5, 56.25) * mm});
            skLineSegment(sketch, "E7.58.0.1", {"start": v(41.5, -34.75) * mm, "end": v(42.5, -34.75) * mm});
            skLineSegment(sketch, "E7.58.0.2", {"start": v(41.5, 56.25) * mm, "end": v(41.5, -34.75) * mm});
            skLineSegment(sketch, "E7.58.0.3", {"start": v(42.5, 56.25) * mm, "end": v(42.5, -34.75) * mm});
            skLineSegment(sketch, "E7.59.0.0", {"start": v(43.5, 56.25) * mm, "end": v(44.5, 56.25) * mm});
            skLineSegment(sketch, "E7.59.0.1", {"start": v(43.5, -34.75) * mm, "end": v(44.5, -34.75) * mm});
            skLineSegment(sketch, "E7.59.0.2", {"start": v(43.5, 56.25) * mm, "end": v(43.5, -34.75) * mm});
            skLineSegment(sketch, "E7.59.0.3", {"start": v(44.5, 56.25) * mm, "end": v(44.5, -34.75) * mm});
            skLineSegment(sketch, "E7.60.0.0", {"start": v(45.5, 56.25) * mm, "end": v(46.5, 56.25) * mm});
            skLineSegment(sketch, "E7.60.0.1", {"start": v(45.5, -34.75) * mm, "end": v(46.5, -34.75) * mm});
            skLineSegment(sketch, "E7.60.0.2", {"start": v(45.5, 56.25) * mm, "end": v(45.5, -34.75) * mm});
            skLineSegment(sketch, "E7.60.0.3", {"start": v(46.5, 56.25) * mm, "end": v(46.5, -34.75) * mm});
            skLineSegment(sketch, "E7.61.0.0", {"start": v(47.5, 56.25) * mm, "end": v(48.5, 56.25) * mm});
            skLineSegment(sketch, "E7.61.0.1", {"start": v(47.5, -34.75) * mm, "end": v(48.5, -34.75) * mm});
            skLineSegment(sketch, "E7.61.0.2", {"start": v(47.5, 56.25) * mm, "end": v(47.5, -34.75) * mm});
            skLineSegment(sketch, "E7.61.0.3", {"start": v(48.5, 56.25) * mm, "end": v(48.5, -34.75) * mm});
            skLineSegment(sketch, "E7.62.0.0", {"start": v(49.5, 56.25) * mm, "end": v(50.5, 56.25) * mm});
            skLineSegment(sketch, "E7.62.0.1", {"start": v(49.5, -34.75) * mm, "end": v(50.5, -34.75) * mm});
            skLineSegment(sketch, "E7.62.0.2", {"start": v(49.5, 56.25) * mm, "end": v(49.5, -34.75) * mm});
            skLineSegment(sketch, "E7.62.0.3", {"start": v(50.5, 56.25) * mm, "end": v(50.5, -34.75) * mm});
            skLineSegment(sketch, "E7.63.0.0", {"start": v(51.5, 56.25) * mm, "end": v(52.5, 56.25) * mm});
            skLineSegment(sketch, "E7.63.0.1", {"start": v(51.5, -34.75) * mm, "end": v(52.5, -34.75) * mm});
            skLineSegment(sketch, "E7.63.0.2", {"start": v(51.5, 56.25) * mm, "end": v(51.5, -34.75) * mm});
            skLineSegment(sketch, "E7.63.0.3", {"start": v(52.5, 56.25) * mm, "end": v(52.5, -34.75) * mm});
            skLineSegment(sketch, "E7.64.0.0", {"start": v(53.5, 56.25) * mm, "end": v(54.5, 56.25) * mm});
            skLineSegment(sketch, "E7.64.0.1", {"start": v(53.5, -34.75) * mm, "end": v(54.5, -34.75) * mm});
            skLineSegment(sketch, "E7.64.0.2", {"start": v(53.5, 56.25) * mm, "end": v(53.5, -34.75) * mm});
            skLineSegment(sketch, "E7.64.0.3", {"start": v(54.5, 56.25) * mm, "end": v(54.5, -34.75) * mm});
            skLineSegment(sketch, "E7.65.0.0", {"start": v(55.5, 56.25) * mm, "end": v(56.5, 56.25) * mm});
            skLineSegment(sketch, "E7.65.0.1", {"start": v(55.5, -34.75) * mm, "end": v(56.5, -34.75) * mm});
            skLineSegment(sketch, "E7.65.0.2", {"start": v(55.5, 56.25) * mm, "end": v(55.5, -34.75) * mm});
            skLineSegment(sketch, "E7.65.0.3", {"start": v(56.5, 56.25) * mm, "end": v(56.5, -34.75) * mm});
            skLineSegment(sketch, "E7.66.0.0", {"start": v(57.5, 56.25) * mm, "end": v(58.5, 56.25) * mm});
            skLineSegment(sketch, "E7.66.0.1", {"start": v(57.5, -34.75) * mm, "end": v(58.5, -34.75) * mm});
            skLineSegment(sketch, "E7.66.0.2", {"start": v(57.5, 56.25) * mm, "end": v(57.5, -34.75) * mm});
            skLineSegment(sketch, "E7.66.0.3", {"start": v(58.5, 56.25) * mm, "end": v(58.5, -34.75) * mm});
            skLineSegment(sketch, "E7.67.0.0", {"start": v(59.5, 56.25) * mm, "end": v(60.5, 56.25) * mm});
            skLineSegment(sketch, "E7.67.0.1", {"start": v(59.5, -34.75) * mm, "end": v(60.5, -34.75) * mm});
            skLineSegment(sketch, "E7.67.0.2", {"start": v(59.5, 56.25) * mm, "end": v(59.5, -34.75) * mm});
            skLineSegment(sketch, "E7.67.0.3", {"start": v(60.5, 56.25) * mm, "end": v(60.5, -34.75) * mm});
            skLineSegment(sketch, "E7.68.0.0", {"start": v(61.5, 56.25) * mm, "end": v(62.5, 56.25) * mm});
            skLineSegment(sketch, "E7.68.0.1", {"start": v(61.5, -34.75) * mm, "end": v(62.5, -34.75) * mm});
            skLineSegment(sketch, "E7.68.0.2", {"start": v(61.5, 56.25) * mm, "end": v(61.5, -34.75) * mm});
            skLineSegment(sketch, "E7.68.0.3", {"start": v(62.5, 56.25) * mm, "end": v(62.5, -34.75) * mm});
            skLineSegment(sketch, "E7.69.0.0", {"start": v(63.5, 56.25) * mm, "end": v(64.5, 56.25) * mm});
            skLineSegment(sketch, "E7.69.0.1", {"start": v(63.5, -34.75) * mm, "end": v(64.5, -34.75) * mm});
            skLineSegment(sketch, "E7.69.0.2", {"start": v(63.5, 56.25) * mm, "end": v(63.5, -34.75) * mm});
            skLineSegment(sketch, "E7.69.0.3", {"start": v(64.5, 56.25) * mm, "end": v(64.5, -34.75) * mm});
            skLineSegment(sketch, "E7.70.0.0", {"start": v(65.5, 56.25) * mm, "end": v(66.5, 56.25) * mm});
            skLineSegment(sketch, "E7.70.0.1", {"start": v(65.5, -34.75) * mm, "end": v(66.5, -34.75) * mm});
            skLineSegment(sketch, "E7.70.0.2", {"start": v(65.5, 56.25) * mm, "end": v(65.5, -34.75) * mm});
            skLineSegment(sketch, "E7.70.0.3", {"start": v(66.5, 56.25) * mm, "end": v(66.5, -34.75) * mm});
            skLineSegment(sketch, "E7.71.0.0", {"start": v(67.5, 56.25) * mm, "end": v(68.5, 56.25) * mm});
            skLineSegment(sketch, "E7.71.0.1", {"start": v(67.5, -34.75) * mm, "end": v(68.5, -34.75) * mm});
            skLineSegment(sketch, "E7.71.0.2", {"start": v(67.5, 56.25) * mm, "end": v(67.5, -34.75) * mm});
            skLineSegment(sketch, "E7.71.0.3", {"start": v(68.5, 56.25) * mm, "end": v(68.5, -34.75) * mm});
            skLineSegment(sketch, "E7.72.0.0", {"start": v(69.5, 56.25) * mm, "end": v(70.5, 56.25) * mm});
            skLineSegment(sketch, "E7.72.0.1", {"start": v(69.5, -34.75) * mm, "end": v(70.5, -34.75) * mm});
            skLineSegment(sketch, "E7.72.0.2", {"start": v(69.5, 56.25) * mm, "end": v(69.5, -34.75) * mm});
            skLineSegment(sketch, "E7.72.0.3", {"start": v(70.5, 56.25) * mm, "end": v(70.5, -34.75) * mm});
            skLineSegment(sketch, "E7.73.0.0", {"start": v(71.5, 56.25) * mm, "end": v(72.5, 56.25) * mm});
            skLineSegment(sketch, "E7.73.0.1", {"start": v(71.5, -34.75) * mm, "end": v(72.5, -34.75) * mm});
            skLineSegment(sketch, "E7.73.0.2", {"start": v(71.5, 56.25) * mm, "end": v(71.5, -34.75) * mm});
            skLineSegment(sketch, "E7.73.0.3", {"start": v(72.5, 56.25) * mm, "end": v(72.5, -34.75) * mm});
            skLineSegment(sketch, "E7.74.0.0", {"start": v(73.5, 56.25) * mm, "end": v(74.5, 56.25) * mm});
            skLineSegment(sketch, "E7.74.0.1", {"start": v(73.5, -34.75) * mm, "end": v(74.5, -34.75) * mm});
            skLineSegment(sketch, "E7.74.0.2", {"start": v(73.5, 56.25) * mm, "end": v(73.5, -34.75) * mm});
            skLineSegment(sketch, "E7.74.0.3", {"start": v(74.5, 56.25) * mm, "end": v(74.5, -34.75) * mm});
            skLineSegment(sketch, "E7.75.0.0", {"start": v(75.5, 56.25) * mm, "end": v(76.5, 56.25) * mm});
            skLineSegment(sketch, "E7.75.0.1", {"start": v(75.5, -34.75) * mm, "end": v(76.5, -34.75) * mm});
            skLineSegment(sketch, "E7.75.0.2", {"start": v(75.5, 56.25) * mm, "end": v(75.5, -34.75) * mm});
            skLineSegment(sketch, "E7.75.0.3", {"start": v(76.5, 56.25) * mm, "end": v(76.5, -34.75) * mm});
            skLineSegment(sketch, "E7.76.0.0", {"start": v(77.5, 56.25) * mm, "end": v(78.5, 56.25) * mm});
            skLineSegment(sketch, "E7.76.0.1", {"start": v(77.5, -34.75) * mm, "end": v(78.5, -34.75) * mm});
            skLineSegment(sketch, "E7.76.0.2", {"start": v(77.5, 56.25) * mm, "end": v(77.5, -34.75) * mm});
            skLineSegment(sketch, "E7.76.0.3", {"start": v(78.5, 56.25) * mm, "end": v(78.5, -34.75) * mm});
            skLineSegment(sketch, "E7.77.0.0", {"start": v(79.5, 56.25) * mm, "end": v(80.5, 56.25) * mm});
            skLineSegment(sketch, "E7.77.0.1", {"start": v(79.5, -34.75) * mm, "end": v(80.5, -34.75) * mm});
            skLineSegment(sketch, "E7.77.0.2", {"start": v(79.5, 56.25) * mm, "end": v(79.5, -34.75) * mm});
            skLineSegment(sketch, "E7.77.0.3", {"start": v(80.5, 56.25) * mm, "end": v(80.5, -34.75) * mm});
            skLineSegment(sketch, "E7.78.0.0", {"start": v(81.5, 56.25) * mm, "end": v(82.5, 56.25) * mm});
            skLineSegment(sketch, "E7.78.0.1", {"start": v(81.5, -34.75) * mm, "end": v(82.5, -34.75) * mm});
            skLineSegment(sketch, "E7.78.0.2", {"start": v(81.5, 56.25) * mm, "end": v(81.5, -34.75) * mm});
            skLineSegment(sketch, "E7.78.0.3", {"start": v(82.5, 56.25) * mm, "end": v(82.5, -34.75) * mm});
            skLineSegment(sketch, "E7.79.0.0", {"start": v(83.5, 56.25) * mm, "end": v(84.5, 56.25) * mm});
            skLineSegment(sketch, "E7.79.0.1", {"start": v(83.5, -34.75) * mm, "end": v(84.5, -34.75) * mm});
            skLineSegment(sketch, "E7.79.0.2", {"start": v(83.5, 56.25) * mm, "end": v(83.5, -34.75) * mm});
            skLineSegment(sketch, "E7.79.0.3", {"start": v(84.5, 56.25) * mm, "end": v(84.5, -34.75) * mm});
            skLineSegment(sketch, "E7.80.0.0", {"start": v(85.5, 56.25) * mm, "end": v(86.5, 56.25) * mm});
            skLineSegment(sketch, "E7.80.0.1", {"start": v(85.5, -34.75) * mm, "end": v(86.5, -34.75) * mm});
            skLineSegment(sketch, "E7.80.0.2", {"start": v(85.5, 56.25) * mm, "end": v(85.5, -34.75) * mm});
            skLineSegment(sketch, "E7.80.0.3", {"start": v(86.5, 56.25) * mm, "end": v(86.5, -34.75) * mm});
            skLineSegment(sketch, "E7.81.0.0", {"start": v(87.5, 56.25) * mm, "end": v(88.5, 56.25) * mm});
            skLineSegment(sketch, "E7.81.0.1", {"start": v(87.5, -34.75) * mm, "end": v(88.5, -34.75) * mm});
            skLineSegment(sketch, "E7.81.0.2", {"start": v(87.5, 56.25) * mm, "end": v(87.5, -34.75) * mm});
            skLineSegment(sketch, "E7.81.0.3", {"start": v(88.5, 56.25) * mm, "end": v(88.5, -34.75) * mm});
            skLineSegment(sketch, "E7.82.0.0", {"start": v(89.5, 56.25) * mm, "end": v(90.5, 56.25) * mm});
            skLineSegment(sketch, "E7.82.0.1", {"start": v(89.5, -34.75) * mm, "end": v(90.5, -34.75) * mm});
            skLineSegment(sketch, "E7.82.0.2", {"start": v(89.5, 56.25) * mm, "end": v(89.5, -34.75) * mm});
            skLineSegment(sketch, "E7.82.0.3", {"start": v(90.5, 56.25) * mm, "end": v(90.5, -34.75) * mm});
            skLineSegment(sketch, "E7.83.0.0", {"start": v(91.5, 56.25) * mm, "end": v(92.5, 56.25) * mm});
            skLineSegment(sketch, "E7.83.0.1", {"start": v(91.5, -34.75) * mm, "end": v(92.5, -34.75) * mm});
            skLineSegment(sketch, "E7.83.0.2", {"start": v(91.5, 56.25) * mm, "end": v(91.5, -34.75) * mm});
            skLineSegment(sketch, "E7.83.0.3", {"start": v(92.5, 56.25) * mm, "end": v(92.5, -34.75) * mm});
            skLineSegment(sketch, "E7.84.0.0", {"start": v(93.5, 56.25) * mm, "end": v(94.5, 56.25) * mm});
            skLineSegment(sketch, "E7.84.0.1", {"start": v(93.5, -34.75) * mm, "end": v(94.5, -34.75) * mm});
            skLineSegment(sketch, "E7.84.0.2", {"start": v(93.5, 56.25) * mm, "end": v(93.5, -34.75) * mm});
            skLineSegment(sketch, "E7.84.0.3", {"start": v(94.5, 56.25) * mm, "end": v(94.5, -34.75) * mm});
            skLineSegment(sketch, "E7.85.0.0", {"start": v(95.5, 56.25) * mm, "end": v(96.5, 56.25) * mm});
            skLineSegment(sketch, "E7.85.0.1", {"start": v(95.5, -34.75) * mm, "end": v(96.5, -34.75) * mm});
            skLineSegment(sketch, "E7.85.0.2", {"start": v(95.5, 56.25) * mm, "end": v(95.5, -34.75) * mm});
            skLineSegment(sketch, "E7.85.0.3", {"start": v(96.5, 56.25) * mm, "end": v(96.5, -34.75) * mm});
            skLineSegment(sketch, "E7.86.0.0", {"start": v(97.5, 56.25) * mm, "end": v(98.5, 56.25) * mm});
            skLineSegment(sketch, "E7.86.0.1", {"start": v(97.5, -34.75) * mm, "end": v(98.5, -34.75) * mm});
            skLineSegment(sketch, "E7.86.0.2", {"start": v(97.5, 56.25) * mm, "end": v(97.5, -34.75) * mm});
            skLineSegment(sketch, "E7.86.0.3", {"start": v(98.5, 56.25) * mm, "end": v(98.5, -34.75) * mm});
            skLineSegment(sketch, "E7.87.0.0", {"start": v(99.5, 56.25) * mm, "end": v(100.5, 56.25) * mm});
            skLineSegment(sketch, "E7.87.0.1", {"start": v(99.5, -34.75) * mm, "end": v(100.5, -34.75) * mm});
            skLineSegment(sketch, "E7.87.0.2", {"start": v(99.5, 56.25) * mm, "end": v(99.5, -34.75) * mm});
            skLineSegment(sketch, "E7.87.0.3", {"start": v(100.5, 56.25) * mm, "end": v(100.5, -34.75) * mm});
            skLineSegment(sketch, "E7.88.0.0", {"start": v(101.5, 56.25) * mm, "end": v(102.5, 56.25) * mm});
            skLineSegment(sketch, "E7.88.0.1", {"start": v(101.5, -34.75) * mm, "end": v(102.5, -34.75) * mm});
            skLineSegment(sketch, "E7.88.0.2", {"start": v(101.5, 56.25) * mm, "end": v(101.5, -34.75) * mm});
            skLineSegment(sketch, "E7.88.0.3", {"start": v(102.5, 56.25) * mm, "end": v(102.5, -34.75) * mm});
            skLineSegment(sketch, "E7.89.0.0", {"start": v(103.5, 56.25) * mm, "end": v(104.5, 56.25) * mm});
            skLineSegment(sketch, "E7.89.0.1", {"start": v(103.5, -34.75) * mm, "end": v(104.5, -34.75) * mm});
            skLineSegment(sketch, "E7.89.0.2", {"start": v(103.5, 56.25) * mm, "end": v(103.5, -34.75) * mm});
            skLineSegment(sketch, "E7.89.0.3", {"start": v(104.5, 56.25) * mm, "end": v(104.5, -34.75) * mm});
            skLineSegment(sketch, "E7.direction1", {"start": v(-74.5, -34.75) * mm, "end": v(-72.5, -34.75) * mm, "construction": true});
            skSolve(sketch);
        }
        {
            var Q0;
            Q0 = qSketchRegion(id + "F4", true);
            extrude(context, id + "F5", {"entities" : qUnion([Q0]), "operationType" : NewBodyOperationType.REMOVE, "oppositeDirection" : true, "depth" : 19 * mm, "offsetDistance" : 25 * mm});
        }
    });
